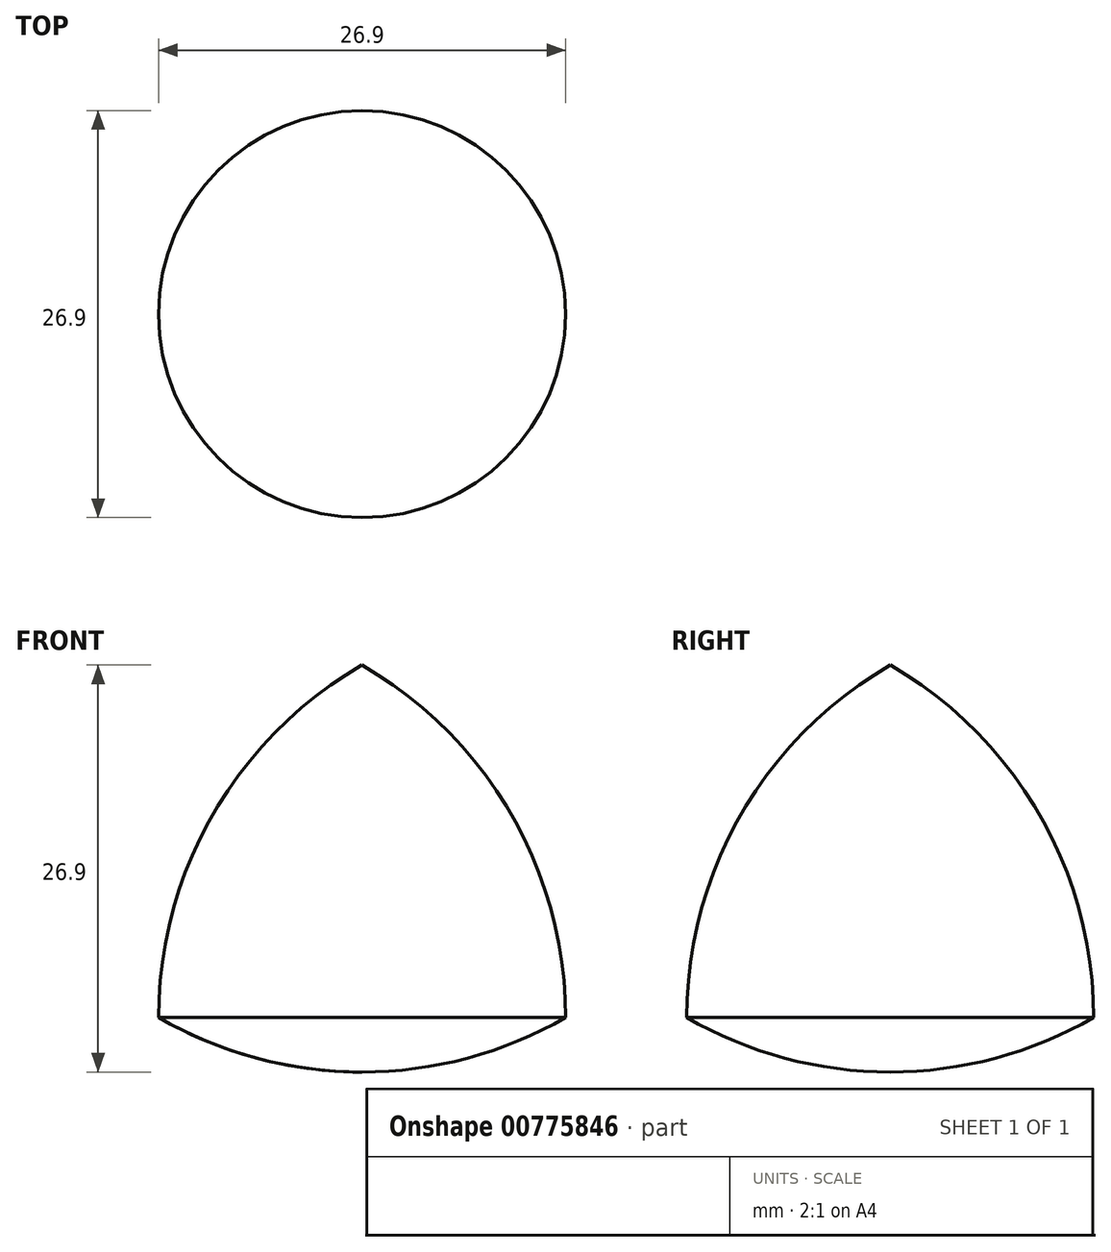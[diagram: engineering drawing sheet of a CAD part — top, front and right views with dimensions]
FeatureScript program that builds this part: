
annotation { "Feature Type Name" : "Feature", "Feature Type Description" : "" }
export const myFeature = defineFeature(function(context is Context, id is Id, definition is map)
    precondition{}
    {
        {
            var Q0;
            Q0=qCreatedBy(makeId("Front.planeOp"),FACE);
            var sketch = newSketch(context, id + "F0", { "sketchPlane" : qUnion([Q0])});
            skArc(sketch, "E0", {"start": v(13.45, 0) * mm, "mid": v(9.85, 13.45) * mm, "end": v(0, 23.3) * mm});
            skArc(sketch, "E1", {"start": v(0, -3.6) * mm, "mid": v(6.96, -2.69) * mm, "end": v(13.45, 0) * mm});
            skLineSegment(sketch, "E2", {"start": v(0, 23.3) * mm, "end": v(0, -3.6) * mm});
            skPoint(sketch, "E3.orphan", {"position": v(0, 25.68) * mm});
            skSolve(sketch);
        }
        {
            var Q0;
            Q0=makeQuery(id+"F0.imprint","IMPRINT",FACE,{"disambiguationData":[TD([[makeQuery(id+"F0.imprint","IMPRINT",EDGE,{"derivedFrom":sQuery(id+"F0.wireOp",EDGE,"E0")}),1.0]])]});
            var Q1;
            Q1=sQuery(id+"F0.wireOp",EDGE,"E2");
            revolve(context, id + "F1", {"surfaceOperationType" : NewSurfaceOperationType.NEW, "entities" : qUnion([Q0]), "axis" : qUnion([Q1]), "revolveType" : RevolveType.FULL});
        }
    });
